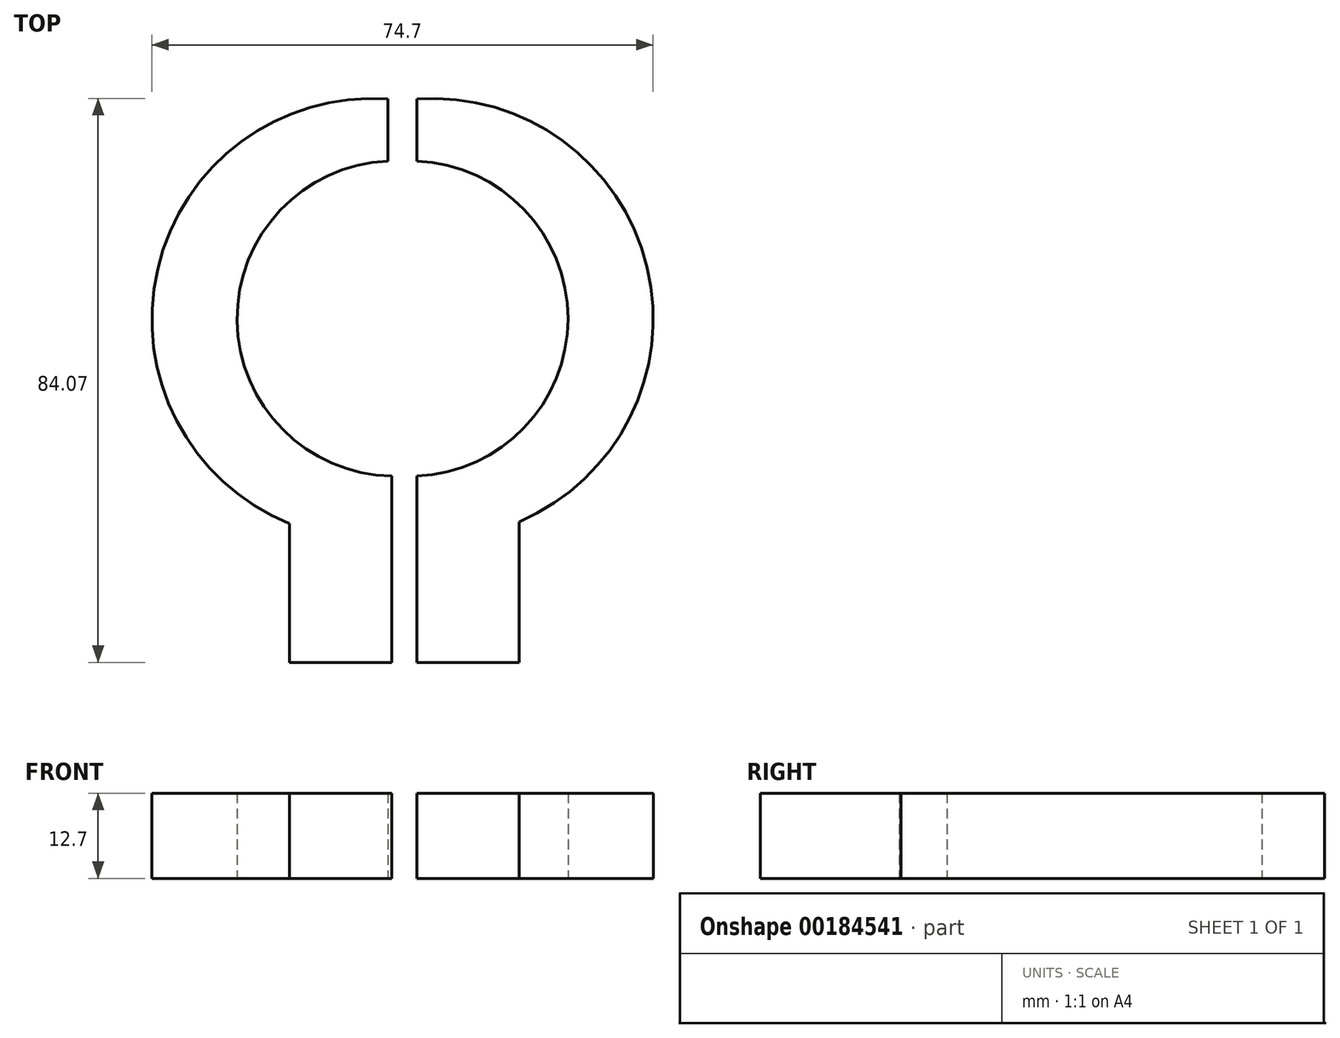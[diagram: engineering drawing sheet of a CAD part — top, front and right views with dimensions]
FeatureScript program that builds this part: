
annotation { "Feature Type Name" : "Feature", "Feature Type Description" : "" }
export const myFeature = defineFeature(function(context is Context, id is Id, definition is map)
    precondition{}
    {
        {
            var Q0;
            Q0=qCreatedBy(makeId("Top.planeOp"),FACE);
            var sketch = newSketch(context, id + "F0", { "sketchPlane" : qUnion([Q0])});
            skArc(sketch, "E0", {"start": v(0, -25.2) * mm, "mid": v(22.53, -1.73) * mm, "end": v(0, 21.74) * mm});
            skArc(sketch, "E1", {"start": v(0, -34.56) * mm, "mid": v(35.23, -1.77) * mm, "end": v(0, 31.01) * mm});
            skLineSegment(sketch, "E2", {"start": v(0, 21.74) * mm, "end": v(0, 31.01) * mm});
            skLineSegment(sketch, "E3", {"start": v(0, -25.2) * mm, "end": v(0, -34.56) * mm});
            skLineSegment(sketch, "E4", {"start": v(0, -34.56) * mm, "end": v(0, -52.97) * mm});
            skLineSegment(sketch, "E5", {"start": v(0, -52.97) * mm, "end": v(15.24, -52.97) * mm});
            skLineSegment(sketch, "E6", {"start": v(15.24, -52.97) * mm, "end": v(15.24, -34.56) * mm});
            skLineSegment(sketch, "E7", {"start": v(15.24, -34.56) * mm, "end": v(15.24, -32.02) * mm});
            skArc(sketch, "E8", {"start": v(-4.28, 21.74) * mm, "mid": v(-26.77, -2) * mm, "end": v(-3.7, -25.2) * mm});
            skLineSegment(sketch, "E9", {"start": v(-3.7, -25.2) * mm, "end": v(-3.7, -52.97) * mm});
            skLineSegment(sketch, "E10", {"start": v(-3.7, -52.97) * mm, "end": v(-18.95, -52.97) * mm});
            skLineSegment(sketch, "E11", {"start": v(-18.95, -52.97) * mm, "end": v(-18.95, -32.02) * mm});
            skLineSegment(sketch, "E12", {"start": v(-4.28, 21.74) * mm, "end": v(-4.28, 31.01) * mm});
            skArc(sketch, "E13", {"start": v(-4.28, 31.01) * mm, "mid": v(-39.47, -2.08) * mm, "end": v(-3.7, -34.56) * mm});
            skSolve(sketch);
        }
        {
            var Q0;
            Q0=makeQuery(id+"F0.imprint","IMPRINT",FACE,{"disambiguationData":[TD([[makeQuery(id+"F0.imprint","IMPRINT",EDGE,{"derivedFrom":sQuery(id+"F0.wireOp",EDGE,"E0")}),-1.0]])]});
            var Q1;
            {var subQ0=sQuery(id+"F0.wireOp",EDGE,"E4");Q1=makeQuery(id+"F0.imprint","IMPRINT",FACE,{"disambiguationData":[TD([[makeQuery(id+"F0.imprint","IMPRINT",EDGE,{"derivedFrom":subQ0}),1.0]])]});}
            var Q2;
            {var subQ4=sQuery(id+"F0.wireOp",EDGE,"E8");Q2=makeQuery(id+"F0.imprint","IMPRINT",FACE,{"disambiguationData":[TD([[makeQuery(id+"F0.imprint","IMPRINT",EDGE,{"derivedFrom":subQ4}),-1.0]])]});}
            var Q3;
            {var subQ0=sQuery(id+"F0.wireOp",EDGE,"E10");Q3=makeQuery(id+"F0.imprint","IMPRINT",FACE,{"disambiguationData":[TD([[makeQuery(id+"F0.imprint","IMPRINT",EDGE,{"derivedFrom":subQ0}),-1.0]])]});}
            extrude(context, id + "F1", {"entities" : qUnion([Q0, Q1, Q2, Q3]), "depth" : 12.7 * mm});
        }
    });
